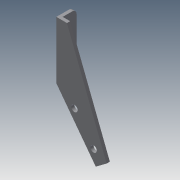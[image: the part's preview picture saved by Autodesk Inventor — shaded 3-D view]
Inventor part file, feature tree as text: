
AUTODESK INVENTOR PART (.ipt)
format: ipt  version: 2015 (Build 190159000, 159)  size: 154,624 bytes
history: native  units: mm
features: sketch x12, extrude x7, fillet x2
ambient origin geometry x8: Origin, YZ Plane, XZ Plane, XY Plane, X Axis, Y Axis, Z Axis, Center Point
bodies: Solid1 (feature_tree)
feature tree (21):
  sketch  "Sketch1"  dims[d4=3.0mm d5=3.0mm d6=2.0mm d7=0.0mm]
  extrude  "Extrusion1"  Depth=2.0mm TaperAngle=0.0deg
  extrude  "Extrusion2"  Depth=2.0mm TaperAngle=0.0deg
  extrude  "Extrusion3"  Depth=2.0mm TaperAngle=0.0deg
  sketch  "Sketch5"  dims[d21=10.0mm d22=0.0mm d23=0.5mm d24=0.0mm]
  extrude  "Extrusion4"  Depth=2.0mm TaperAngle=0.0deg
  sketch  "Sketch7"  dims[d28=2.0mm]
  sketch  "Sketch8"
  extrude  "Extrusion5"  Depth=10.0mm TaperAngle=0.0deg
  extrude  "Extrusion6"  Depth=2.0mm
  extrude  "Extrusion7"  [1 undecoded]
  fillet  "Fillet1"  [1 undecoded]
  fillet  "Fillet2"  [1 undecoded]
  sketch  "Sketch12"
  sketch  "Sketch2"  dims[d8=10.0mm d11=2.0mm d12=0.0mm]
  sketch  "Sketch3"  dims[d13=5.0mm d14=2.0mm d15=0.0mm]
  sketch  "Sketch4"  dims[d16=2.0mm d17=6.0mm d18=0.0mm]
  sketch  "Sketch6"  dims[d25=0.5mm d26=0.0mm d27=2.0mm]
  sketch  "Sketch9"
  sketch  "Sketch10"
  sketch  "Sketch11"
note: 3 required parameter values undecoded (feature->parameter linkage not recoverable at this tier; creation-order binding heuristic only, values carry confidence <= 0.55)
